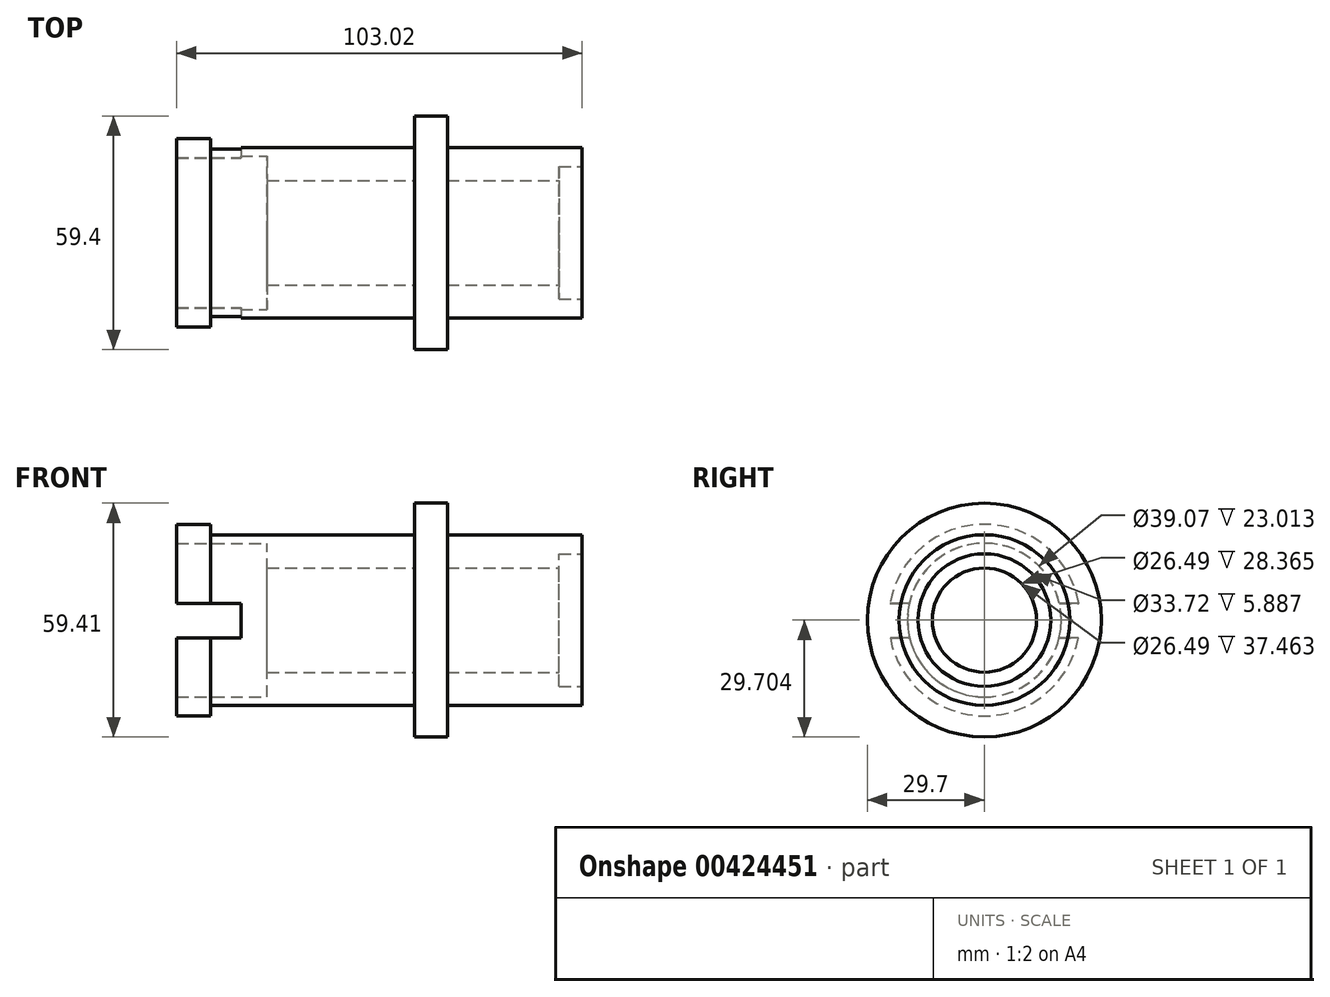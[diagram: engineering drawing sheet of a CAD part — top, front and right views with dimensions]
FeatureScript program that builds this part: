
annotation { "Feature Type Name" : "Feature", "Feature Type Description" : "" }
export const myFeature = defineFeature(function(context is Context, id is Id, definition is map)
    precondition{}
    {
        {
            var Q0;
            Q0=qCreatedBy(makeId("Front.planeOp"),FACE);
            var sketch = newSketch(context, id + "F0", { "sketchPlane" : qUnion([Q0])});
            skLineSegment(sketch, "E0", {"start": v(0, 0) * mm, "end": v(0, -13.25) * mm});
            skLineSegment(sketch, "E1", {"start": v(0, -13.25) * mm, "end": v(-8.3, -13.25) * mm});
            skLineSegment(sketch, "E2", {"start": v(-8.3, -13.25) * mm, "end": v(-8.3, 0) * mm});
            skLineSegment(sketch, "E3", {"start": v(-8.3, 0) * mm, "end": v(-45.76, 0) * mm});
            skLineSegment(sketch, "E4", {"start": v(-45.76, 0) * mm, "end": v(-45.76, 6.29) * mm});
            skLineSegment(sketch, "E5", {"start": v(-45.76, 6.29) * mm, "end": v(-68.77, 6.29) * mm});
            skLineSegment(sketch, "E6", {"start": v(-68.77, 6.29) * mm, "end": v(-68.77, 11.1) * mm});
            skLineSegment(sketch, "E7", {"start": v(-68.77, 11.1) * mm, "end": v(-60.2, 11.1) * mm});
            skLineSegment(sketch, "E8", {"start": v(-60.2, 11.1) * mm, "end": v(-60.2, 8.43) * mm});
            skLineSegment(sketch, "E9", {"start": v(-60.2, 8.43) * mm, "end": v(-8.3, 8.43) * mm});
            skLineSegment(sketch, "E10", {"start": v(-8.3, 8.43) * mm, "end": v(-8.3, 16.46) * mm});
            skLineSegment(sketch, "E11", {"start": v(-8.3, 16.46) * mm, "end": v(0, 16.46) * mm});
            skLineSegment(sketch, "E12", {"start": v(0, 16.46) * mm, "end": v(0, 8.43) * mm});
            skLineSegment(sketch, "E13", {"start": v(0, 8.43) * mm, "end": v(34.25, 8.43) * mm});
            skLineSegment(sketch, "E14", {"start": v(34.25, 8.43) * mm, "end": v(34.25, 3.61) * mm});
            skLineSegment(sketch, "E15", {"start": v(34.25, 3.61) * mm, "end": v(28.36, 3.61) * mm});
            skLineSegment(sketch, "E16", {"start": v(28.36, 3.61) * mm, "end": v(28.36, 0) * mm});
            skLineSegment(sketch, "E17", {"start": v(28.36, 0) * mm, "end": v(0, 0) * mm});
            skSolve(sketch);
        }
        {
            var Q0;
            Q0=makeQuery(id+"F0.imprint","IMPRINT",FACE,{"disambiguationData":[TD([[makeQuery(id+"F0.imprint","IMPRINT",EDGE,{"derivedFrom":sQuery(id+"F0.wireOp",EDGE,"E0")}),-1.0]])]});
            var Q1;
            Q1=sQuery(id+"F0.wireOp",EDGE,"E1");
            revolve(context, id + "F1", {"entities" : qUnion([Q0]), "axis" : qUnion([Q1]), "revolveType" : RevolveType.FULL});
        }
        {
            var Q0;
            Q0=qCreatedBy(makeId("Front.planeOp"),FACE);
            var sketch = newSketch(context, id + "F2", { "sketchPlane" : qUnion([Q0])});
            skLineSegment(sketch, "E18.bottom", {"start": v(-72.52, -8.96) * mm, "end": v(-52.45, -8.96) * mm});
            skLineSegment(sketch, "E18.top", {"start": v(-72.52, -17.8) * mm, "end": v(-52.45, -17.8) * mm});
            skLineSegment(sketch, "E18.left", {"start": v(-72.52, -8.96) * mm, "end": v(-72.52, -17.8) * mm});
            skLineSegment(sketch, "E18.right", {"start": v(-52.45, -8.96) * mm, "end": v(-52.45, -17.8) * mm});
            skSolve(sketch);
        }
        {
            var Q0;
            Q0=makeQuery(id+"F2.imprint","IMPRINT",FACE,{"disambiguationData":[TD([[makeQuery(id+"F2.imprint","IMPRINT",EDGE,{"derivedFrom":sQuery(id+"F2.wireOp",EDGE,"E18.bottom")}),-1.0]])]});
            extrude(context, id + "F3", {"entities" : qUnion([Q0]), "operationType" : NewBodyOperationType.REMOVE, "endBound" : BoundingType.SYMMETRIC, "oppositeDirection" : true, "depth" : 12700 * mm});
        }
    });
